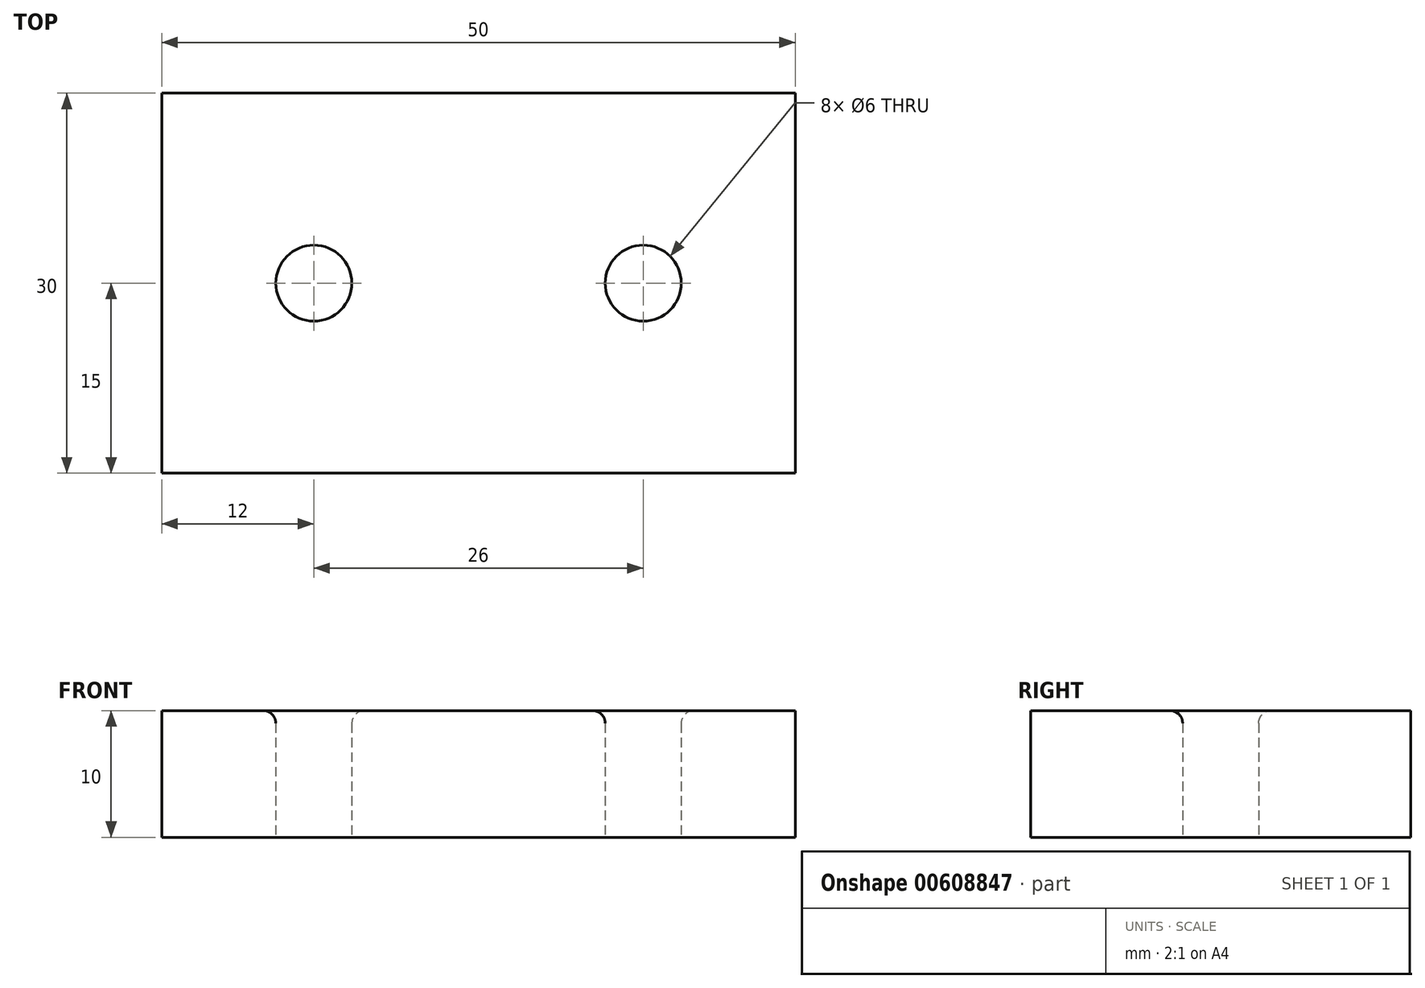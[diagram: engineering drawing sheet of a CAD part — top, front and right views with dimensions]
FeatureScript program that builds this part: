
annotation { "Feature Type Name" : "Feature", "Feature Type Description" : "" }
export const myFeature = defineFeature(function(context is Context, id is Id, definition is map)
    precondition{}
    {
        {
            var Q0;
            Q0=qCreatedBy(makeId("Top.planeOp"),FACE);
            var sketch = newSketch(context, id + "F0", { "sketchPlane" : qUnion([Q0])});
            skLineSegment(sketch, "E0.bottom", {"start": v(0, 0) * mm, "end": v(-50, 0) * mm});
            skLineSegment(sketch, "E0.top", {"start": v(0, 30) * mm, "end": v(-50, 30) * mm});
            skLineSegment(sketch, "E0.left", {"start": v(0, 0) * mm, "end": v(0, 30) * mm});
            skLineSegment(sketch, "E0.right", {"start": v(-50, 0) * mm, "end": v(-50, 30) * mm});
            skCircle(sketch, "E1", {"center": v(-38, 15) * mm, "radius": 3 * mm});
            skCircle(sketch, "E2", {"center": v(-12, 15) * mm, "radius": 3 * mm});
            skSolve(sketch);
        }
        {
            var Q0;
            Q0 = qSketchRegion(id + "F0", true);
            extrude(context, id + "F1", {"entities" : qUnion([Q0]), "depth" : 10 * mm, "offsetDistance" : 25 * mm});
        }
        {
            var Q0;
            Q0=makeQuery(id+"F1.opExtrude","CAP_EDGE",EDGE,{"disambiguationData":[OSD([sQuery(id+"F0.wireOp",EDGE,"E1")])],"isStart":false});
            var Q1;
            Q1=makeQuery(id+"F1.opExtrude","CAP_EDGE",EDGE,{"disambiguationData":[OSD([sQuery(id+"F0.wireOp",EDGE,"E2")])],"isStart":false});
            fillet(context, id + "F2", {"entities" : qUnion([Q0, Q1]), "radius" : 1 * mm, "tangentPropagation" : true, "allowEdgeOverflow" : false});
        }
    });
